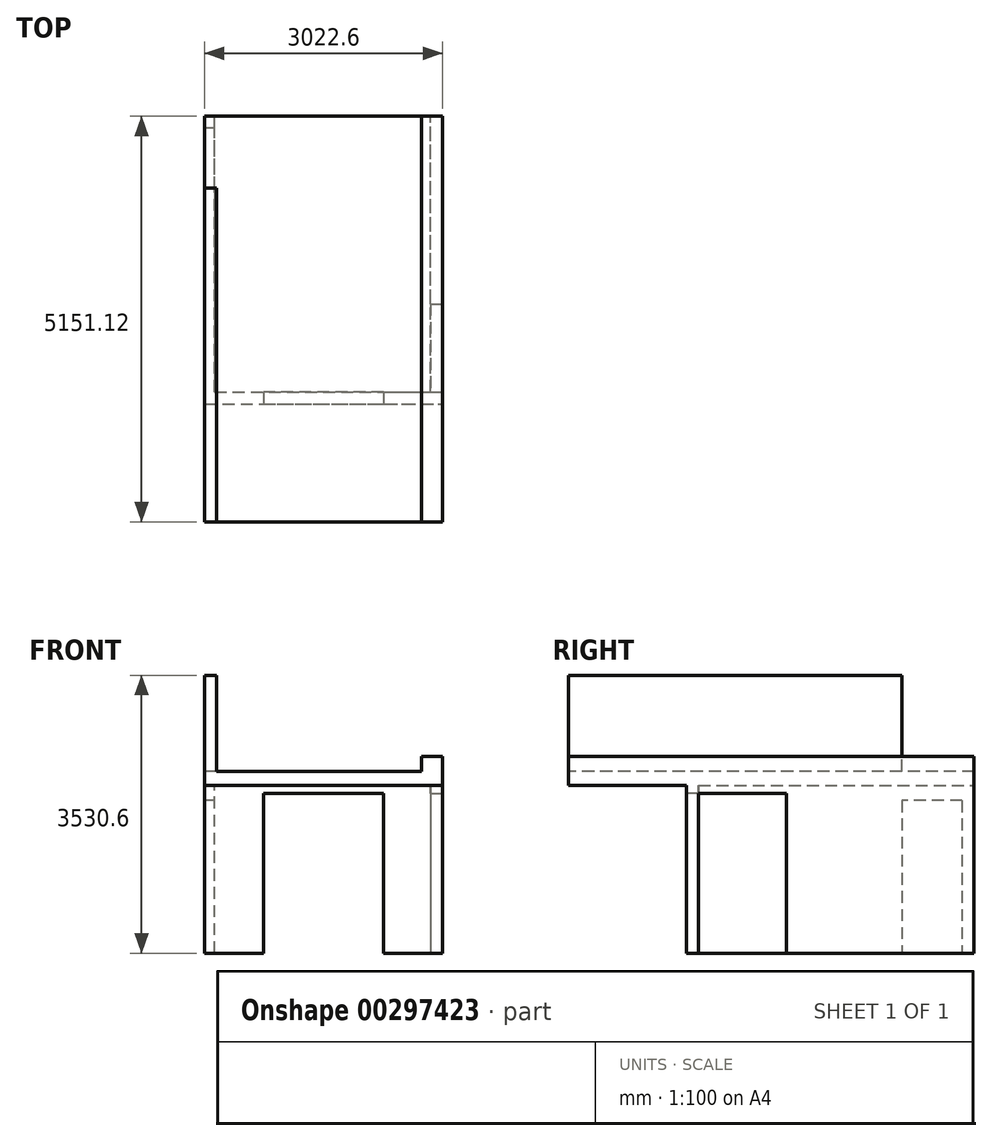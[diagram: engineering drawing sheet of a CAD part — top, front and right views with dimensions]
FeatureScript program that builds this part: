
annotation { "Feature Type Name" : "Feature", "Feature Type Description" : "" }
export const myFeature = defineFeature(function(context is Context, id is Id, definition is map)
    precondition{}
    {
        {
            var Q0;
            Q0=qCreatedBy(makeId("Top.planeOp"),FACE);
            var sketch = newSketch(context, id + "F0", { "sketchPlane" : qUnion([Q0])});
            skLineSegment(sketch, "E0.bottom", {"start": v(0, 0) * mm, "end": v(3835.4, 0) * mm});
            skLineSegment(sketch, "E0.top", {"start": v(0, 3652.52) * mm, "end": v(3835.4, 3652.52) * mm});
            skLineSegment(sketch, "E0.left", {"start": v(0, 0) * mm, "end": v(0, 3652.52) * mm});
            skLineSegment(sketch, "E0.right", {"start": v(3835.4, 0) * mm, "end": v(3835.4, 3652.52) * mm});
            skLineSegment(sketch, "E1.0", {"start": v(152.4, 152.4) * mm, "end": v(152.4, 3500.12) * mm});
            skLineSegment(sketch, "E1.1", {"start": v(152.4, 152.4) * mm, "end": v(3683, 152.4) * mm});
            skLineSegment(sketch, "E1.2", {"start": v(3683, 152.4) * mm, "end": v(3683, 3500.12) * mm});
            skLineSegment(sketch, "E1.3", {"start": v(152.4, 3500.12) * mm, "end": v(3683, 3500.12) * mm});
            skSolve(sketch);
        }
        {
            var Q0;
            Q0=qSketchRegion(id+"F0",true);
            extrude(context, id + "F1", {"entities" : qUnion([Q0]), "oppositeDirection" : true, "depth" : 2133.6 * mm, "offsetDistance" : 25.4 * mm});
        }
        {
            var Q0;
            Q0=makeQuery(id+"F1.opExtrude","SWEPT_FACE",FACE,{"disambiguationData":[OSD([sQuery(id+"F0.wireOp",EDGE,"E0.bottom")])]});
            var sketch = newSketch(context, id + "F2", { "sketchPlane" : qUnion([Q0])});
            skLineSegment(sketch, "E2.bottom", {"start": v(0, 0) * mm, "end": v(3835.4, 0) * mm});
            skLineSegment(sketch, "E2.top", {"start": v(0, 177.8) * mm, "end": v(3835.4, 177.8) * mm});
            skLineSegment(sketch, "E2.left", {"start": v(0, 0) * mm, "end": v(0, 177.8) * mm});
            skLineSegment(sketch, "E2.right", {"start": v(3835.4, 0) * mm, "end": v(3835.4, 177.8) * mm});
            skSolve(sketch);
        }
        {
            var Q0;
            Q0=makeQuery(id+"F2.imprint","IMPRINT",FACE,{"disambiguationData":[TD([[makeQuery(id+"F2.imprint","IMPRINT",EDGE,{"derivedFrom":sQuery(id+"F2.wireOp",EDGE,"E2.bottom")}),1.0]])]});
            var Q1;
            Q1=makeQuery(id+"F1.opExtrude","SWEPT_FACE",FACE,{"disambiguationData":[OSD([sQuery(id+"F0.wireOp",EDGE,"E0.top")])]});
            extrude(context, id + "F3", {"entities" : qUnion([Q0]), "operationType" : NewBodyOperationType.ADD, "endBound" : BoundingType.UP_TO_SURFACE, "oppositeDirection" : true, "endBoundEntityFace" : qUnion([Q1]), "depth" : 25.4 * mm});
        }
        {
            var Q0;
            Q0=makeQuery(id+"F3.boolean.opBoolean","MERGE",FACE,{"derivedFrom":[makeQuery(id+"F1.opExtrude","SWEPT_FACE",FACE,{"disambiguationData":[OSD([sQuery(id+"F0.wireOp",EDGE,"E0.left")])]}),makeQuery(id+"F3.opExtrude","SWEPT_FACE",FACE,{"disambiguationData":[OSD([sQuery(id+"F2.wireOp",EDGE,"E2.left")])]})]});
            var sketch = newSketch(context, id + "F4", { "sketchPlane" : qUnion([Q0])});
            skLineSegment(sketch, "E3.0", {"start": v(-3500.12, 0) * mm, "end": v(-152.4, 0) * mm});
            skLineSegment(sketch, "E3.1", {"start": v(-3500.12, -2133.6) * mm, "end": v(-3500.12, 0) * mm});
            skLineSegment(sketch, "E3.2", {"start": v(-152.4, -2133.6) * mm, "end": v(-3500.12, -2133.6) * mm});
            skLineSegment(sketch, "E3.3", {"start": v(-152.4, 0) * mm, "end": v(-152.4, -2133.6) * mm});
            skSolve(sketch);
        }
        {
            var Q0;
            Q0=qSketchRegion(id+"F4",true);
            var Q1;
            Q1=makeQuery(id+"F1.opExtrude","SWEPT_FACE",FACE,{"disambiguationData":[OSD([sQuery(id+"F0.wireOp",EDGE,"E1.0")])]});
            extrude(context, id + "F5", {"entities" : qUnion([Q0]), "operationType" : NewBodyOperationType.REMOVE, "endBound" : BoundingType.UP_TO_SURFACE, "oppositeDirection" : true, "endBoundEntityFace" : qUnion([Q1]), "depth" : 25.4 * mm});
        }
        {
            var Q0;
            Q0=makeQuery(id+"F3.opExtrude","SWEPT_FACE",FACE,{"disambiguationData":[OSD([sQuery(id+"F2.wireOp",EDGE,"E2.top")])]});
            var sketch = newSketch(context, id + "F6", { "sketchPlane" : qUnion([Q0])});
            skLineSegment(sketch, "E4.bottom", {"start": v(0, 3652.52) * mm, "end": v(3835.4, 3652.52) * mm});
            skLineSegment(sketch, "E4.top", {"start": v(0, -1498.6) * mm, "end": v(3835.4, -1498.6) * mm});
            skLineSegment(sketch, "E4.left", {"start": v(0, 3652.52) * mm, "end": v(0, -1498.6) * mm});
            skLineSegment(sketch, "E4.right", {"start": v(3835.4, 3652.52) * mm, "end": v(3835.4, -1498.6) * mm});
            skSolve(sketch);
        }
        {
            var Q0;
            Q0=qSketchRegion(id+"F6",true);
            var Q1;
            Q1=makeQuery(id+"F5.boolean.opBoolean","MERGE",FACE,{"derivedFrom":[makeQuery(id+"F3.opExtrude","SWEPT_FACE",FACE,{"disambiguationData":[OSD([sQuery(id+"F2.wireOp",EDGE,"E2.bottom")])]}),makeQuery(id+"F5.opExtrude","SWEPT_FACE",FACE,{"disambiguationData":[OSD([sQuery(id+"F4.wireOp",EDGE,"E3.0")])]})]});
            extrude(context, id + "F7", {"entities" : qUnion([Q0]), "operationType" : NewBodyOperationType.ADD, "endBound" : BoundingType.UP_TO_SURFACE, "oppositeDirection" : true, "endBoundEntityFace" : qUnion([Q1]), "depth" : 25.4 * mm});
        }
        {
            var Q0;
            Q0=makeQuery(id+"F7.boolean.opBoolean","MERGE",FACE,{"derivedFrom":[makeQuery(id+"F3.boolean.opBoolean","MERGE",FACE,{"derivedFrom":[makeQuery(id+"F1.opExtrude","SWEPT_FACE",FACE,{"disambiguationData":[OSD([sQuery(id+"F0.wireOp",EDGE,"E0.left")])]}),makeQuery(id+"F3.opExtrude","SWEPT_FACE",FACE,{"disambiguationData":[OSD([sQuery(id+"F2.wireOp",EDGE,"E2.left")])]})]}),makeQuery(id+"F7.opExtrude","SWEPT_FACE",FACE,{"disambiguationData":[OSD([sQuery(id+"F6.wireOp",EDGE,"E4.left")])]})]});
            var sketch = newSketch(context, id + "F8", { "sketchPlane" : qUnion([Q0])});
            skLineSegment(sketch, "E5.bottom", {"start": v(-3500.12, -2133.6) * mm, "end": v(1498.6, -2133.6) * mm});
            skLineSegment(sketch, "E5.top", {"start": v(-3500.12, 177.8) * mm, "end": v(1498.6, 177.8) * mm});
            skLineSegment(sketch, "E5.left", {"start": v(-3500.12, -2133.6) * mm, "end": v(-3500.12, 177.8) * mm});
            skLineSegment(sketch, "E5.right", {"start": v(1498.6, -2133.6) * mm, "end": v(1498.6, 177.8) * mm});
            skSolve(sketch);
        }
        {
            var Q0;
            {var subQ1=makeQuery(id+"F3.boolean.opBoolean","MERGE",EDGE,{"derivedFrom":[makeQuery(id+"F1.opExtrude","SWEPT_EDGE",EDGE,{"disambiguationData":[OSD([sQuery(id+"F0.wireOp",EDGE,"E0.bottom"),sQuery(id+"F0.wireOp",EDGE,"E0.left")])]}),makeQuery(id+"F3.opExtrude","CAP_EDGE",EDGE,{"disambiguationData":[OSD([sQuery(id+"F2.wireOp",EDGE,"E2.left")])],"isStart":true})]});Q0=makeQuery(id+"F8.imprint","IMPRINT",FACE,{"disambiguationData":[TD([[makeQuery(id+"F8.imprint","IMPRINT",EDGE,{"derivedFrom":subQ1}),-1.0]])]});}
            var Q1;
            {var subQ7=makeQuery(id+"F5.boolean.opBoolean","COPY",EDGE,{"derivedFrom":makeQuery(id+"F5.opExtrude","CAP_EDGE",EDGE,{"disambiguationData":[OSD([sQuery(id+"F4.wireOp",EDGE,"E3.0")])],"isStart":true})});Q1=makeQuery(id+"F8.imprint","IMPRINT",FACE,{"disambiguationData":[TD([[makeQuery(id+"F8.imprint","IMPRINT",EDGE,{"derivedFrom":subQ7}),-1.0]])]});}
            var Q2;
            {var subQ6=sQuery(id+"F8.wireOp",EDGE,"E5.top");Q2=makeQuery(id+"F8.imprint","IMPRINT",FACE,{"disambiguationData":[TD([[makeQuery(id+"F8.imprint","IMPRINT",EDGE,{"derivedFrom":subQ6}),-1.0]])]});}
            extrude(context, id + "F9", {"entities" : qUnion([Q0, Q1, Q2]), "operationType" : NewBodyOperationType.REMOVE, "oppositeDirection" : true, "depth" : 812.8 * mm});
        }
        {
            var Q0;
            Q0=makeQuery(id+"F9.boolean.opBoolean","COPY",FACE,{"derivedFrom":makeQuery(id+"F9.opExtrude","CAP_FACE",FACE,{"disambiguationData":[OSD([sQuery(id+"F8.wireOp",EDGE,"E5.bottom"),sQuery(id+"F8.wireOp",EDGE,"E5.top"),sQuery(id+"F8.wireOp",EDGE,"E5.left"),sQuery(id+"F8.wireOp",EDGE,"E5.right")])],"isStart":false})});
            var sketch = newSketch(context, id + "F10", { "sketchPlane" : qUnion([Q0])});
            skLineSegment(sketch, "E6.bottom", {"start": v(-3500.12, 177.8) * mm, "end": v(0, 177.8) * mm});
            skLineSegment(sketch, "E6.top", {"start": v(-3500.12, -2133.6) * mm, "end": v(0, -2133.6) * mm});
            skLineSegment(sketch, "E6.left", {"start": v(-3500.12, 177.8) * mm, "end": v(-3500.12, -2133.6) * mm});
            skLineSegment(sketch, "E6.right", {"start": v(0, 177.8) * mm, "end": v(0, -2133.6) * mm});
            skSolve(sketch);
        }
        {
            var Q0;
            Q0=qSketchRegion(id+"F10",true);
            extrude(context, id + "F11", {"entities" : qUnion([Q0]), "operationType" : NewBodyOperationType.ADD, "oppositeDirection" : true, "depth" : 127 * mm});
        }
        {
            var Q0;
            Q0=makeQuery(id+"F3.boolean.opBoolean","MERGE",FACE,{"derivedFrom":[makeQuery(id+"F1.opExtrude","SWEPT_FACE",FACE,{"disambiguationData":[OSD([sQuery(id+"F0.wireOp",EDGE,"E0.bottom")])]}),makeQuery(id+"F3.opExtrude","CAP_FACE",FACE,{"disambiguationData":[OSD([sQuery(id+"F2.wireOp",EDGE,"E2.bottom"),sQuery(id+"F2.wireOp",EDGE,"E2.top"),sQuery(id+"F2.wireOp",EDGE,"E2.left"),sQuery(id+"F2.wireOp",EDGE,"E2.right")])],"isStart":true})]});
            var sketch = newSketch(context, id + "F12", { "sketchPlane" : qUnion([Q0])});
            skLineSegment(sketch, "E7.bottom", {"start": v(1562.1, -2133.6) * mm, "end": v(3086.1, -2133.6) * mm});
            skLineSegment(sketch, "E7.top", {"start": v(1562.1, -101.6) * mm, "end": v(3086.1, -101.6) * mm});
            skLineSegment(sketch, "E7.left", {"start": v(1562.1, -2133.6) * mm, "end": v(1562.1, -101.6) * mm});
            skLineSegment(sketch, "E7.right", {"start": v(3086.1, -2133.6) * mm, "end": v(3086.1, -101.6) * mm});
            skSolve(sketch);
        }
        {
            var Q0;
            Q0 = qSketchRegion(id + "F12", true);
            extrude(context, id + "F13", {"entities" : qUnion([Q0]), "operationType" : NewBodyOperationType.REMOVE, "endBound" : BoundingType.UP_TO_NEXT, "oppositeDirection" : true, "depth" : 25.4 * mm});
        }
        {
            var Q0;
            Q0=makeQuery(id+"F7.boolean.opBoolean","MERGE",FACE,{"derivedFrom":[makeQuery(id+"F3.boolean.opBoolean","MERGE",FACE,{"derivedFrom":[makeQuery(id+"F1.opExtrude","SWEPT_FACE",FACE,{"disambiguationData":[OSD([sQuery(id+"F0.wireOp",EDGE,"E0.right")])]}),makeQuery(id+"F3.opExtrude","SWEPT_FACE",FACE,{"disambiguationData":[OSD([sQuery(id+"F2.wireOp",EDGE,"E2.right")])]})]}),makeQuery(id+"F7.opExtrude","SWEPT_FACE",FACE,{"disambiguationData":[OSD([sQuery(id+"F6.wireOp",EDGE,"E4.right")])]})]});
            var sketch = newSketch(context, id + "F14", { "sketchPlane" : qUnion([Q0])});
            skLineSegment(sketch, "E8.bottom", {"start": v(152.4, -2133.6) * mm, "end": v(1270, -2133.6) * mm});
            skLineSegment(sketch, "E8.top", {"start": v(152.4, -101.6) * mm, "end": v(1270, -101.6) * mm});
            skLineSegment(sketch, "E8.left", {"start": v(152.4, -2133.6) * mm, "end": v(152.4, -101.6) * mm});
            skLineSegment(sketch, "E8.right", {"start": v(1270, -2133.6) * mm, "end": v(1270, -101.6) * mm});
            skSolve(sketch);
        }
        {
            var Q0;
            Q0 = qSketchRegion(id + "F14", true);
            extrude(context, id + "F15", {"entities" : qUnion([Q0]), "operationType" : NewBodyOperationType.REMOVE, "endBound" : BoundingType.UP_TO_NEXT, "oppositeDirection" : true, "depth" : 25.4 * mm});
        }
        {
            var Q0;
            {var subQ0=sQuery(id+"F0.wireOp",EDGE,"E1.3");var subQ1=sQuery(id+"F0.wireOp",EDGE,"E1.2");Q0=makeQuery(id+"F11.boolean.opBoolean","SPLIT",FACE,{"disambiguationData":[TD([makeQuery(id+"F1.opExtrude","SWEPT_FACE",FACE,{"disambiguationData":[OSD([subQ1])]})])],"derivedFrom":makeQuery(id+"F9.boolean.opBoolean","MERGE",FACE,{"derivedFrom":[makeQuery(id+"F5.boolean.opBoolean","MERGE",FACE,{"derivedFrom":[makeQuery(id+"F1.opExtrude","SWEPT_FACE",FACE,{"disambiguationData":[OSD([subQ0])]}),makeQuery(id+"F5.opExtrude","SWEPT_FACE",FACE,{"disambiguationData":[OSD([sQuery(id+"F4.wireOp",EDGE,"E3.1")])]})]}),makeQuery(id+"F9.opExtrude","SWEPT_FACE",FACE,{"disambiguationData":[OSD([sQuery(id+"F8.wireOp",EDGE,"E5.left")])]})]})});}
            var sketch = newSketch(context, id + "F16", { "sketchPlane" : qUnion([Q0])});
            skLineSegment(sketch, "E9.bottom", {"start": v(939.8, -2133.6) * mm, "end": v(3683, -2133.6) * mm});
            skLineSegment(sketch, "E9.top", {"start": v(939.8, 0) * mm, "end": v(3683, 0) * mm});
            skLineSegment(sketch, "E9.left", {"start": v(939.8, -2133.6) * mm, "end": v(939.8, 0) * mm});
            skLineSegment(sketch, "E9.right", {"start": v(3683, -2133.6) * mm, "end": v(3683, 0) * mm});
            skSolve(sketch);
        }
        {
            var Q0;
            Q0 = qSketchRegion(id + "F16", true);
            extrude(context, id + "F17", {"entities" : qUnion([Q0]), "operationType" : NewBodyOperationType.REMOVE, "endBound" : BoundingType.UP_TO_NEXT, "oppositeDirection" : true, "depth" : 25.4 * mm});
        }
        {
            var Q0;
            {var subQ0=sQuery(id+"F0.wireOp",EDGE,"E0.left");var subQ2=sQuery(id+"F0.wireOp",EDGE,"E1.3");var subQ4=sQuery(id+"F8.wireOp",EDGE,"E5.left");Q0=makeQuery(id+"F11.boolean.opBoolean","SPLIT",FACE,{"disambiguationData":[TD([makeQuery(id+"F1.opExtrude","SWEPT_FACE",FACE,{"disambiguationData":[OSD([subQ0])]})])],"derivedFrom":makeQuery(id+"F9.boolean.opBoolean","MERGE",FACE,{"derivedFrom":[makeQuery(id+"F5.boolean.opBoolean","MERGE",FACE,{"derivedFrom":[makeQuery(id+"F1.opExtrude","SWEPT_FACE",FACE,{"disambiguationData":[OSD([subQ2])]}),makeQuery(id+"F5.opExtrude","SWEPT_FACE",FACE,{"disambiguationData":[OSD([sQuery(id+"F4.wireOp",EDGE,"E3.1")])]})]}),makeQuery(id+"F9.opExtrude","SWEPT_FACE",FACE,{"disambiguationData":[OSD([subQ4])]})]})});}
            var sketch = newSketch(context, id + "F18", { "sketchPlane" : qUnion([Q0])});
            skLineSegment(sketch, "E10.bottom", {"start": v(0, -2133.6) * mm, "end": v(812.8, -2133.6) * mm});
            skLineSegment(sketch, "E10.top", {"start": v(0, 177.8) * mm, "end": v(812.8, 177.8) * mm});
            skLineSegment(sketch, "E10.left", {"start": v(0, -2133.6) * mm, "end": v(0, 177.8) * mm});
            skLineSegment(sketch, "E10.right", {"start": v(812.8, -2133.6) * mm, "end": v(812.8, 177.8) * mm});
            skSolve(sketch);
        }
        {
            var Q0;
            Q0 = qSketchRegion(id + "F18", true);
            extrude(context, id + "F19", {"entities" : qUnion([Q0]), "operationType" : NewBodyOperationType.REMOVE, "endBound" : BoundingType.UP_TO_NEXT, "oppositeDirection" : true, "depth" : 25.4 * mm});
        }
        {
            var Q0;
            Q0=makeQuery(id+"F19.boolean.opBoolean","MERGE",FACE,{"derivedFrom":[makeQuery(id+"F11.boolean.opBoolean","MERGE",FACE,{"derivedFrom":[makeQuery(id+"F9.boolean.opBoolean","COPY",FACE,{"derivedFrom":makeQuery(id+"F9.opExtrude","CAP_FACE",FACE,{"disambiguationData":[OSD([sQuery(id+"F8.wireOp",EDGE,"E5.bottom"),sQuery(id+"F8.wireOp",EDGE,"E5.top"),sQuery(id+"F8.wireOp",EDGE,"E5.left"),sQuery(id+"F8.wireOp",EDGE,"E5.right")])],"isStart":false})}),makeQuery(id+"F11.opExtrude","CAP_FACE",FACE,{"disambiguationData":[OSD([sQuery(id+"F10.wireOp",EDGE,"E6.bottom"),sQuery(id+"F10.wireOp",EDGE,"E6.top"),sQuery(id+"F10.wireOp",EDGE,"E6.left"),sQuery(id+"F10.wireOp",EDGE,"E6.right")])],"isStart":true})]}),makeQuery(id+"F19.opExtrude","SWEPT_FACE",FACE,{"disambiguationData":[OSD([sQuery(id+"F18.wireOp",EDGE,"E10.right")])]})]});
            var sketch = newSketch(context, id + "F20", { "sketchPlane" : qUnion([Q0])});
            skLineSegment(sketch, "E11.bottom", {"start": v(1498.6, 177.8) * mm, "end": v(-2738.12, 177.8) * mm});
            skLineSegment(sketch, "E11.top", {"start": v(1498.6, 1397) * mm, "end": v(-2738.12, 1397) * mm});
            skLineSegment(sketch, "E11.left", {"start": v(1498.6, 177.8) * mm, "end": v(1498.6, 1397) * mm});
            skLineSegment(sketch, "E11.right", {"start": v(-2738.12, 177.8) * mm, "end": v(-2738.12, 1397) * mm});
            skSolve(sketch);
        }
        {
            var Q0;
            Q0 = qSketchRegion(id + "F20", true);
            extrude(context, id + "F21", {"entities" : qUnion([Q0]), "operationType" : NewBodyOperationType.ADD, "oppositeDirection" : true, "depth" : 152.4 * mm});
        }
        {
            var Q0;
            Q0=makeQuery(id+"F21.boolean.opBoolean","MERGE",FACE,{"derivedFrom":[makeQuery(id+"F19.boolean.opBoolean","MERGE",FACE,{"derivedFrom":[makeQuery(id+"F11.boolean.opBoolean","MERGE",FACE,{"derivedFrom":[makeQuery(id+"F9.boolean.opBoolean","COPY",FACE,{"derivedFrom":makeQuery(id+"F9.opExtrude","CAP_FACE",FACE,{"disambiguationData":[OSD([sQuery(id+"F8.wireOp",EDGE,"E5.bottom"),sQuery(id+"F8.wireOp",EDGE,"E5.top"),sQuery(id+"F8.wireOp",EDGE,"E5.left"),sQuery(id+"F8.wireOp",EDGE,"E5.right")])],"isStart":false})}),makeQuery(id+"F11.opExtrude","CAP_FACE",FACE,{"disambiguationData":[OSD([sQuery(id+"F10.wireOp",EDGE,"E6.bottom"),sQuery(id+"F10.wireOp",EDGE,"E6.top"),sQuery(id+"F10.wireOp",EDGE,"E6.left"),sQuery(id+"F10.wireOp",EDGE,"E6.right")])],"isStart":true})]}),makeQuery(id+"F19.opExtrude","SWEPT_FACE",FACE,{"disambiguationData":[OSD([sQuery(id+"F18.wireOp",EDGE,"E10.right")])]})]}),makeQuery(id+"F21.opExtrude","CAP_FACE",FACE,{"disambiguationData":[OSD([sQuery(id+"F20.wireOp",EDGE,"E11.bottom"),sQuery(id+"F20.wireOp",EDGE,"E11.top"),sQuery(id+"F20.wireOp",EDGE,"E11.left"),sQuery(id+"F20.wireOp",EDGE,"E11.right")])],"isStart":true})]});
            var sketch = newSketch(context, id + "F22", { "sketchPlane" : qUnion([Q0])});
            skLineSegment(sketch, "E12", {"start": v(-203.2, -2133.6) * mm, "end": v(-2738.12, 0) * mm});
            skLineSegment(sketch, "E13", {"start": v(-2738.12, 0) * mm, "end": v(-3652.52, 0) * mm});
            skLineSegment(sketch, "E14", {"start": v(-3652.52, 0) * mm, "end": v(-3652.52, -2133.6) * mm});
            skLineSegment(sketch, "E15", {"start": v(-3652.52, -2133.6) * mm, "end": v(-203.2, -2133.6) * mm});
            skSolve(sketch);
        }
        {
            var Q0;
            Q0 = qSketchRegion(id + "F22", true);
            extrude(context, id + "F23", {"entities" : qUnion([Q0]), "operationType" : NewBodyOperationType.REMOVE, "oppositeDirection" : true, "depth" : 152.4 * mm, "offsetDistance" : 25.4 * mm});
        }
        {
            var Q0;
            Q0=makeQuery(id+"F21.boolean.opBoolean","MERGE",FACE,{"derivedFrom":[makeQuery(id+"F19.boolean.opBoolean","MERGE",FACE,{"derivedFrom":[makeQuery(id+"F11.boolean.opBoolean","MERGE",FACE,{"derivedFrom":[makeQuery(id+"F9.boolean.opBoolean","COPY",FACE,{"derivedFrom":makeQuery(id+"F9.opExtrude","CAP_FACE",FACE,{"disambiguationData":[OSD([sQuery(id+"F8.wireOp",EDGE,"E5.bottom"),sQuery(id+"F8.wireOp",EDGE,"E5.top"),sQuery(id+"F8.wireOp",EDGE,"E5.left"),sQuery(id+"F8.wireOp",EDGE,"E5.right")])],"isStart":false})}),makeQuery(id+"F11.opExtrude","CAP_FACE",FACE,{"disambiguationData":[OSD([sQuery(id+"F10.wireOp",EDGE,"E6.bottom"),sQuery(id+"F10.wireOp",EDGE,"E6.top"),sQuery(id+"F10.wireOp",EDGE,"E6.left"),sQuery(id+"F10.wireOp",EDGE,"E6.right")])],"isStart":true})]}),makeQuery(id+"F19.opExtrude","SWEPT_FACE",FACE,{"disambiguationData":[OSD([sQuery(id+"F18.wireOp",EDGE,"E10.right")])]})]}),makeQuery(id+"F21.opExtrude","CAP_FACE",FACE,{"disambiguationData":[OSD([sQuery(id+"F20.wireOp",EDGE,"E11.bottom"),sQuery(id+"F20.wireOp",EDGE,"E11.top"),sQuery(id+"F20.wireOp",EDGE,"E11.left"),sQuery(id+"F20.wireOp",EDGE,"E11.right")])],"isStart":true})]});
            var sketch = newSketch(context, id + "F24", { "sketchPlane" : qUnion([Q0])});
            skLineSegment(sketch, "E16.bottom", {"start": v(-3652.52, 0) * mm, "end": v(-3500.12, 0) * mm});
            skLineSegment(sketch, "E16.top", {"start": v(-3652.52, -2133.6) * mm, "end": v(-3500.12, -2133.6) * mm});
            skLineSegment(sketch, "E16.left", {"start": v(-3652.52, 0) * mm, "end": v(-3652.52, -2133.6) * mm});
            skLineSegment(sketch, "E16.right", {"start": v(-3500.12, -193.68) * mm, "end": v(-3500.12, -2133.6) * mm});
            skLineSegment(sketch, "E17.left", {"start": v(-2738.12, -193.67) * mm, "end": v(-2738.12, -2133.6) * mm});
            skLineSegment(sketch, "E18", {"start": v(-2738.12, 0) * mm, "end": v(-203.2, -2133.6) * mm});
            skLineSegment(sketch, "E19", {"start": v(-2738.12, -2133.6) * mm, "end": v(-203.2, -2133.6) * mm});
            skLineSegment(sketch, "E20", {"start": v(-3500.12, -193.68) * mm, "end": v(-2738.12, -193.67) * mm});
            skLineSegment(sketch, "E21", {"start": v(-3500.12, 0) * mm, "end": v(-2738.12, 0) * mm});
            skSolve(sketch);
        }
        {
            var Q0;
            Q0 = qSketchRegion(id + "F24", true);
            var Q1;
            Q1=makeQuery(id+"F17.boolean.opBoolean","MERGE",FACE,{"derivedFrom":[makeQuery(id+"F11.opExtrude","CAP_FACE",FACE,{"disambiguationData":[OSD([sQuery(id+"F10.wireOp",EDGE,"E6.bottom"),sQuery(id+"F10.wireOp",EDGE,"E6.top"),sQuery(id+"F10.wireOp",EDGE,"E6.left"),sQuery(id+"F10.wireOp",EDGE,"E6.right")])],"isStart":false}),makeQuery(id+"F17.opExtrude","SWEPT_FACE",FACE,{"disambiguationData":[OSD([sQuery(id+"F16.wireOp",EDGE,"E9.left")])]})]});
            extrude(context, id + "F25", {"entities" : qUnion([Q0]), "operationType" : NewBodyOperationType.ADD, "endBound" : BoundingType.UP_TO_SURFACE, "oppositeDirection" : true, "endBoundEntityFace" : qUnion([Q1]), "depth" : 152.4 * mm, "offsetDistance" : 25.4 * mm});
        }
        {
            var Q0;
            Q0=makeQuery(id+"F21.boolean.opBoolean","MERGE",FACE,{"derivedFrom":[makeQuery(id+"F7.opExtrude","SWEPT_FACE",FACE,{"disambiguationData":[OSD([sQuery(id+"F6.wireOp",EDGE,"E4.top")])]}),makeQuery(id+"F21.opExtrude","SWEPT_FACE",FACE,{"disambiguationData":[OSD([sQuery(id+"F20.wireOp",EDGE,"E11.left")])]})]});
            var sketch = newSketch(context, id + "F26", { "sketchPlane" : qUnion([Q0])});
            skLineSegment(sketch, "E22.bottom", {"start": v(3835.4, 177.8) * mm, "end": v(3568.7, 177.8) * mm});
            skLineSegment(sketch, "E22.top", {"start": v(3835.4, 368.3) * mm, "end": v(3568.7, 368.3) * mm});
            skLineSegment(sketch, "E22.left", {"start": v(3835.4, 177.8) * mm, "end": v(3835.4, 368.3) * mm});
            skLineSegment(sketch, "E22.right", {"start": v(3568.7, 177.8) * mm, "end": v(3568.7, 368.3) * mm});
            skSolve(sketch);
        }
        {
            var Q0;
            Q0 = qSketchRegion(id + "F26", true);
            var Q1;
            {var subQ0=sQuery(id+"F0.wireOp",EDGE,"E0.top");Q1=makeQuery(id+"F25.boolean.opBoolean","MERGE",FACE,{"derivedFrom":[makeQuery(id+"F3.boolean.opBoolean","MERGE",FACE,{"derivedFrom":[makeQuery(id+"F1.opExtrude","SWEPT_FACE",FACE,{"disambiguationData":[OSD([subQ0])]}),makeQuery(id+"F3.opExtrude","CAP_FACE",FACE,{"disambiguationData":[OSD([subQ0])],"isStart":false})]}),makeQuery(id+"F25.opExtrude","SWEPT_FACE",FACE,{"disambiguationData":[OSD([sQuery(id+"F24.wireOp",EDGE,"E16.left")])]})]});}
            extrude(context, id + "F27", {"entities" : qUnion([Q0]), "operationType" : NewBodyOperationType.ADD, "endBound" : BoundingType.UP_TO_SURFACE, "oppositeDirection" : true, "depth" : 25.4 * mm, "endBoundEntityFace" : qUnion([Q1]), "offsetDistance" : 25.4 * mm});
        }
    });
